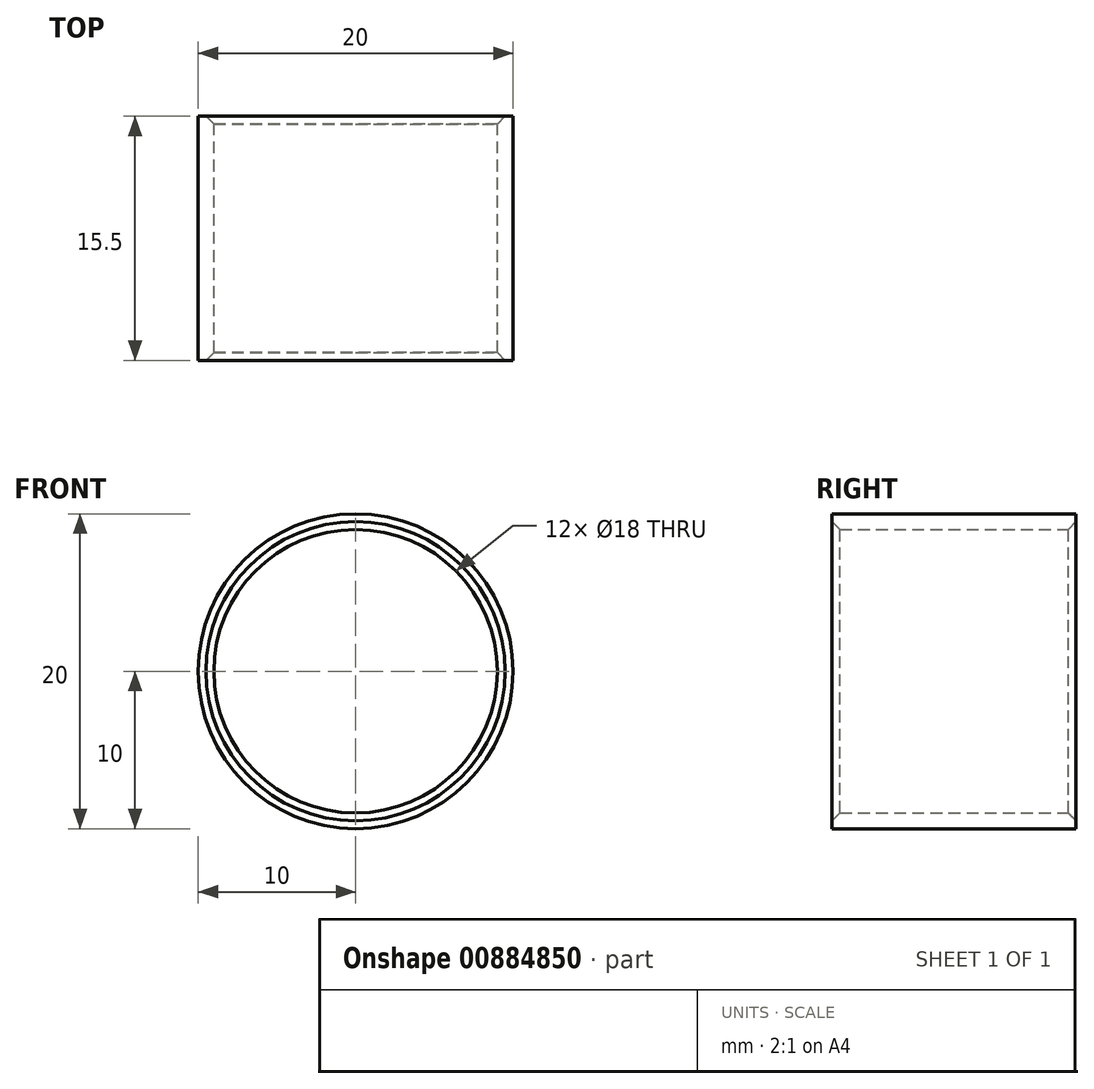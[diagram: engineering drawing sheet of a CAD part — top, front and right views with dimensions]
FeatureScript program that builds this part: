
annotation { "Feature Type Name" : "Feature", "Feature Type Description" : "" }
export const myFeature = defineFeature(function(context is Context, id is Id, definition is map)
    precondition{}
    {
        {
            var Q0;
            Q0=qCreatedBy(makeId("Front.planeOp"),FACE);
            var sketch = newSketch(context, id + "F0", { "sketchPlane" : qUnion([Q0])});
            skCircle(sketch, "E0", {"center": v(0, 0) * mm, "radius": 9 * mm});
            skCircle(sketch, "E1.0", {"center": v(0, 0) * mm, "radius": 10 * mm});
            skSolve(sketch);
        }
        {
            var Q0;
            Q0=makeQuery(id+"F0.imprint","IMPRINT",FACE,{"disambiguationData":[TD([[makeQuery(id+"F0.imprint","IMPRINT",EDGE,{"derivedFrom":sQuery(id+"F0.wireOp",EDGE,"E0")}),-1.0]])]});
            extrude(context, id + "F1", {"entities" : qUnion([Q0]), "depth" : 15.5 * mm, "offsetDistance" : 25 * mm});
        }
        {
            var Q0;
            Q0=makeQuery(id+"F1.opExtrude","SWEPT_FACE",FACE,{"disambiguationData":[OSD([sQuery(id+"F0.wireOp",EDGE,"E0")])]});
            chamfer(context, id + "F2", {"entities" : qUnion([Q0]), "width" : .5 * mm, "tangentPropagation" : true});
        }
    });
